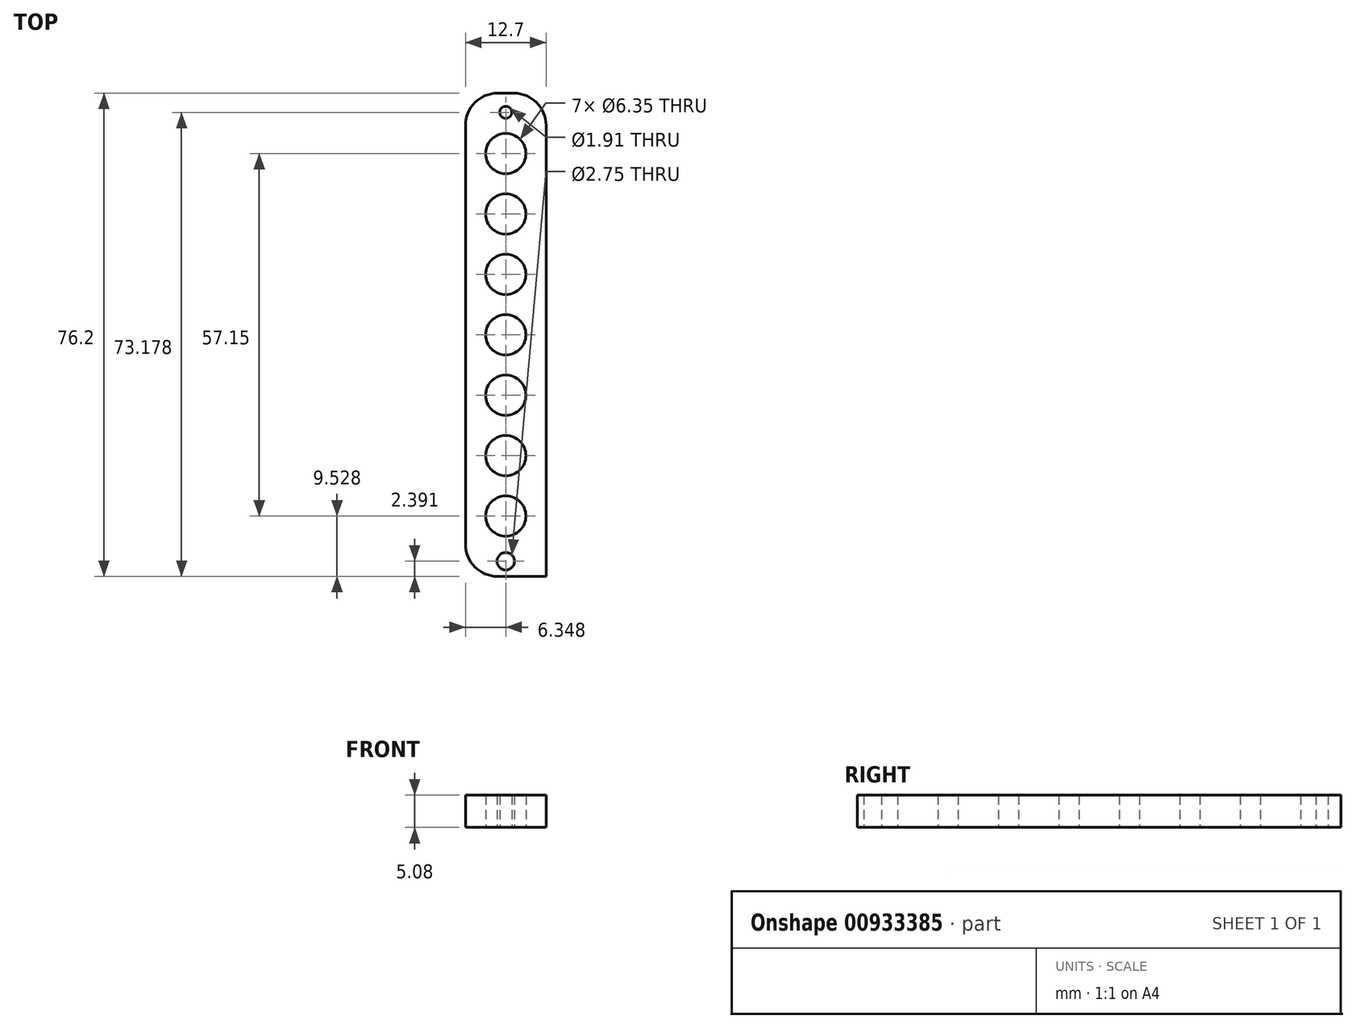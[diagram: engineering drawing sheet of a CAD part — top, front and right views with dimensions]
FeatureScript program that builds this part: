
annotation { "Feature Type Name" : "Feature", "Feature Type Description" : "" }
export const myFeature = defineFeature(function(context is Context, id is Id, definition is map)
    precondition{}
    {
        {
            var Q0;
            Q0=qCreatedBy(makeId("Top.planeOp"),FACE);
            var sketch = newSketch(context, id + "F0", { "sketchPlane" : qUnion([Q0])});
            skLineSegment(sketch, "E0.bottom", {"start": v(18.93, 30.23) * mm, "end": v(31.63, 30.23) * mm});
            skLineSegment(sketch, "E0.top", {"start": v(18.93, -45.97) * mm, "end": v(31.63, -45.97) * mm});
            skLineSegment(sketch, "E0.left", {"start": v(18.93, 30.23) * mm, "end": v(18.93, -45.97) * mm});
            skLineSegment(sketch, "E0.right", {"start": v(31.63, 30.23) * mm, "end": v(31.63, -45.97) * mm});
            skCircle(sketch, "E1", {"center": v(25.28, -7.87) * mm, "radius": 3.18 * mm});
            skCircle(sketch, "E2", {"center": v(25.28, 11.18) * mm, "radius": 3.18 * mm});
            skCircle(sketch, "E3", {"center": v(25.28, -26.92) * mm, "radius": 3.18 * mm});
            skLineSegment(sketch, "E4", {"start": v(25.28, 11.18) * mm, "end": v(25.28, 30.23) * mm});
            skCircle(sketch, "E5", {"center": v(25.28, 20.7) * mm, "radius": 3.18 * mm});
            skLineSegment(sketch, "E6", {"start": v(25.28, 11.18) * mm, "end": v(25.28, -7.87) * mm});
            skCircle(sketch, "E7", {"center": v(25.28, 1.66) * mm, "radius": 3.18 * mm});
            skLineSegment(sketch, "E8", {"start": v(25.28, -7.87) * mm, "end": v(25.28, -26.92) * mm});
            skCircle(sketch, "E9", {"center": v(25.28, -17.4) * mm, "radius": 3.18 * mm});
            skLineSegment(sketch, "E10", {"start": v(25.28, -26.92) * mm, "end": v(25.28, -45.97) * mm});
            skCircle(sketch, "E11", {"center": v(25.28, -36.44) * mm, "radius": 3.18 * mm});
            skCircle(sketch, "E12", {"center": v(25.28, 27.2) * mm, "radius": 0.95 * mm});
            skLineSegment(sketch, "E13", {"start": v(25.28, 30.23) * mm, "end": v(18.93, 30.23) * mm});
            skCircle(sketch, "E14", {"center": v(25.28, -43.58) * mm, "radius": 1.37 * mm});
            skSolve(sketch);
        }
        {
            var Q0;
            Q0 = qSketchRegion(id + "F0", true);
            extrude(context, id + "F1", {"entities" : qUnion([Q0]), "depth" : 5.08 * mm, "offsetDistance" : 25.4 * mm});
        }
        {
            var Q0;
            Q0=makeQuery(id+"F1.opExtrude","SWEPT_EDGE",EDGE,{"disambiguationData":[OSD([sQuery(id+"F0.wireOp",EDGE,"E0.bottom"),sQuery(id+"F0.wireOp",EDGE,"E0.right")])]});
            var Q1;
            Q1=makeQuery(id+"F1.opExtrude","SWEPT_EDGE",EDGE,{"disambiguationData":[OSD([sQuery(id+"F0.wireOp",EDGE,"E0.left"),sQuery(id+"F0.wireOp",EDGE,"E13")])]});
            fillet(context, id + "F2", {"entities" : qUnion([Q0, Q1]), "radius" : 5.08 * mm, "tangentPropagation" : true, "allowEdgeOverflow" : false});
        }
    });
